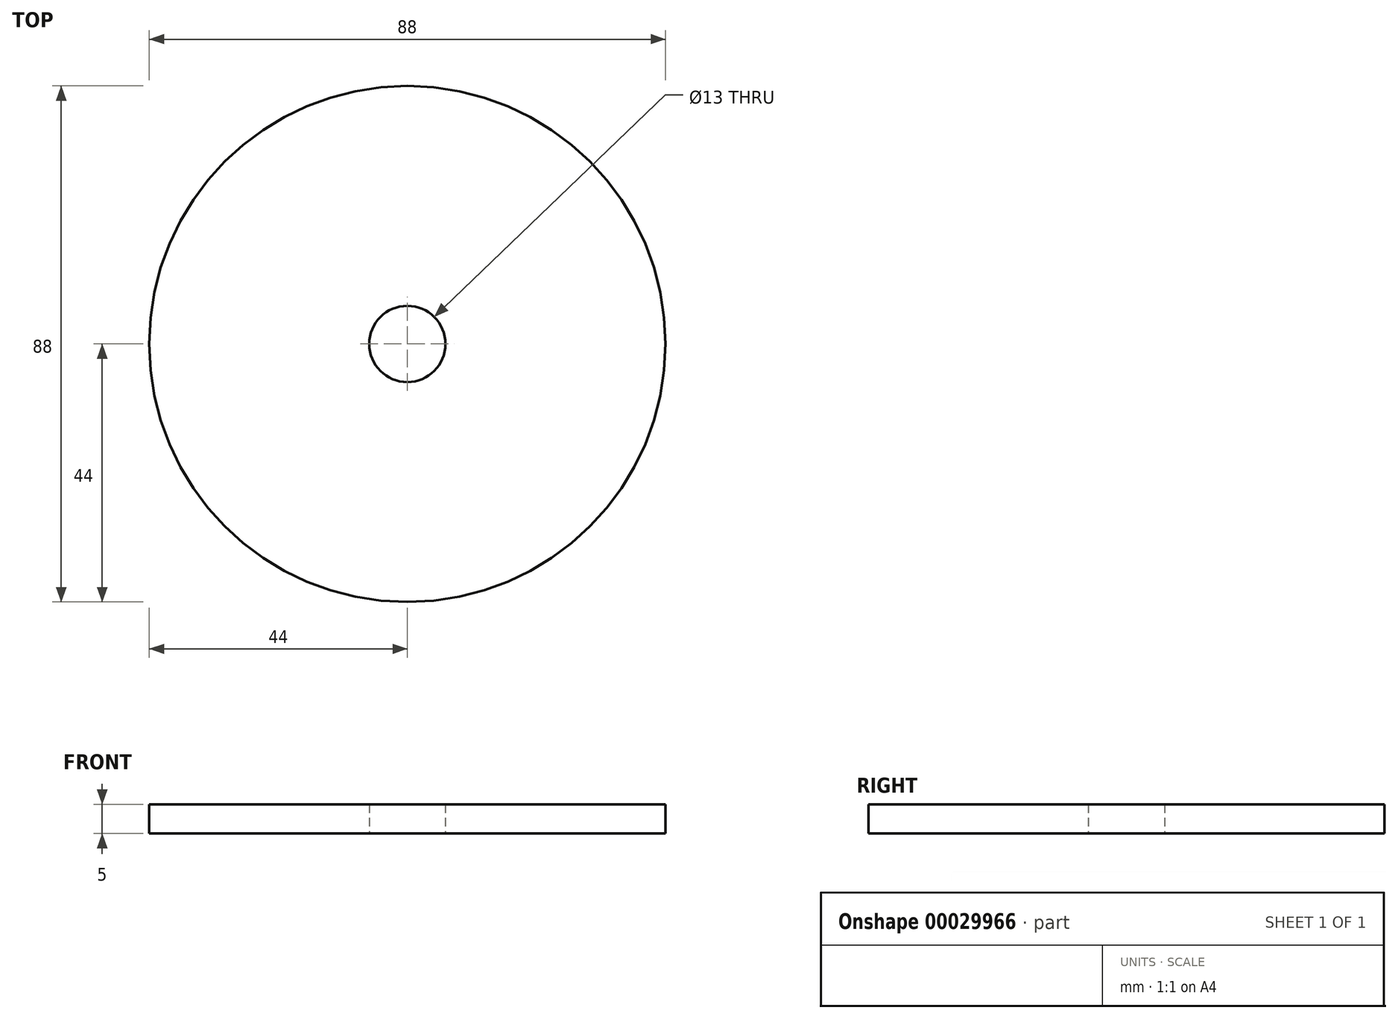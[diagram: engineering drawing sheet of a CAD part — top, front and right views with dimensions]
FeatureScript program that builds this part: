
annotation { "Feature Type Name" : "Feature", "Feature Type Description" : "" }
export const myFeature = defineFeature(function(context is Context, id is Id, definition is map)
    precondition{}
    {
        {
            var Q0;
            Q0=qCreatedBy(makeId("Top.planeOp"),FACE);
            var sketch = newSketch(context, id + "F0", { "sketchPlane" : qUnion([Q0])});
            skCircle(sketch, "E0", {"center": v(0, 0) * mm, "radius": 44 * mm});
            skCircle(sketch, "E1", {"center": v(0, 0) * mm, "radius": 6.5 * mm});
            skSolve(sketch);
        }
        {
            var Q0;
            Q0 = qSketchRegion(id + "F0", true);
            extrude(context, id + "F1", {"entities" : qUnion([Q0]), "depth" : 5 * mm});
        }
    });
